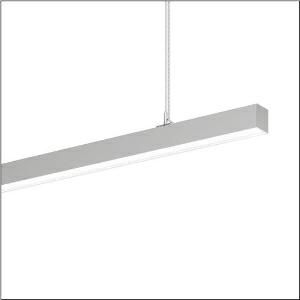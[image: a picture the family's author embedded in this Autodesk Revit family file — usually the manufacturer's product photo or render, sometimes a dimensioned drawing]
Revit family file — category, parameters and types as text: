
# Revit family: silica_21_51mx30dc49sb
name_source: partatom
category: Lighting Fixtures
units: mm (PartAtom-declared; Revit-internal decimal feet)

## family parameters
Cut with Voids When Loaded = No
Host = Face
Light Source = No
Part Type = Normal
Room Calculation Point = No
Round Connector Dimension = Use Diameter
Shared = No

## types (1)
- --- (1 x LED, 10520 lm, 64.1 W, 4000K)
    Apparent Load = 64 VA
    CIE Flux Codes = 47 79 96 57 100
    Color Rendering = 80
    Color Temperature = 4000K
    Default Elevation = 1800 mm
    Description = Silica 21, office luminaire, primary optical cover: cover, of PMMA, opal, light emission: direct/indirect distribution, primary light characteristic: symmetric, installation type: suspended mounting, LED, rated luminous flux: 10.520lm, luminous efficacy: 164lm/W, light colour: 840, colour temperature: 4000K, control gear: DALI 2, with terminal, 3+2-pole, max. 2.5mm², mains connection: 220..240V, AC, 50/60Hz, rated input power: 64.1W, luminaire housing, of aluminium, metallic grey (RAL 9006), length: 3.004mm, width: 53mm, height: 53mm, protection rating (complete): IP20, insulation class (complete): insulation class I (protective earthing), certification: CE, permissible operating ambient temperature: 0..+35°C, standard: EN 50419, packaging unit: 1 piece
    Height = 53 mm
    Lamp = 1 x LED
    Lamp Light Flux = 10520 lm
    Lamp Power = 64.1 W
    Lamp count = 1
    Length = 3004 mm
    Luminous efficacy = 164 lm/W
    Manufacturer = Siteco
    ModVariant = No
    Model = 51MX30DC49SB
    Mounting Place = Ceiling
    Mounting Type = Pendant
    Number of Poles = 1
    OnlyDefault = Yes
    Power Factor = 1
    Product Name = Silica 21
    Product group = office luminaire | ceiling pendant
    ProductGroupID = 903
    Protection Class = Protection class I
    Protection Degree = IP 20
    RLX_Detail_Level = 1
    RLX_Emergency_Light_Flux = 0 lm
    RLX_Emergency_Type = 0
    RLX_Emergency_Type_DB = No
    RlxData = <blob elided: 23253 chars, md5=c67f0d42>
    Socket = socket
    Standby Power = 0 W
    System Light Flux = 10520 lm
    System Power = 64 W
    Type Comments = factory setting: luminous flux: 100 % | dim-lin: 254 | 218 mA
    Type Image = l_1335864.jpg
    URL = http://relux.com
    VarID = @adj_118827
    Voltage = 0 V
    Weight = 0.00 kg
    Width = 53 mm

## geometry (parser evidence)
native form markers: Blend x4, Sweep x12
no freeform markers — native parametric forms only
